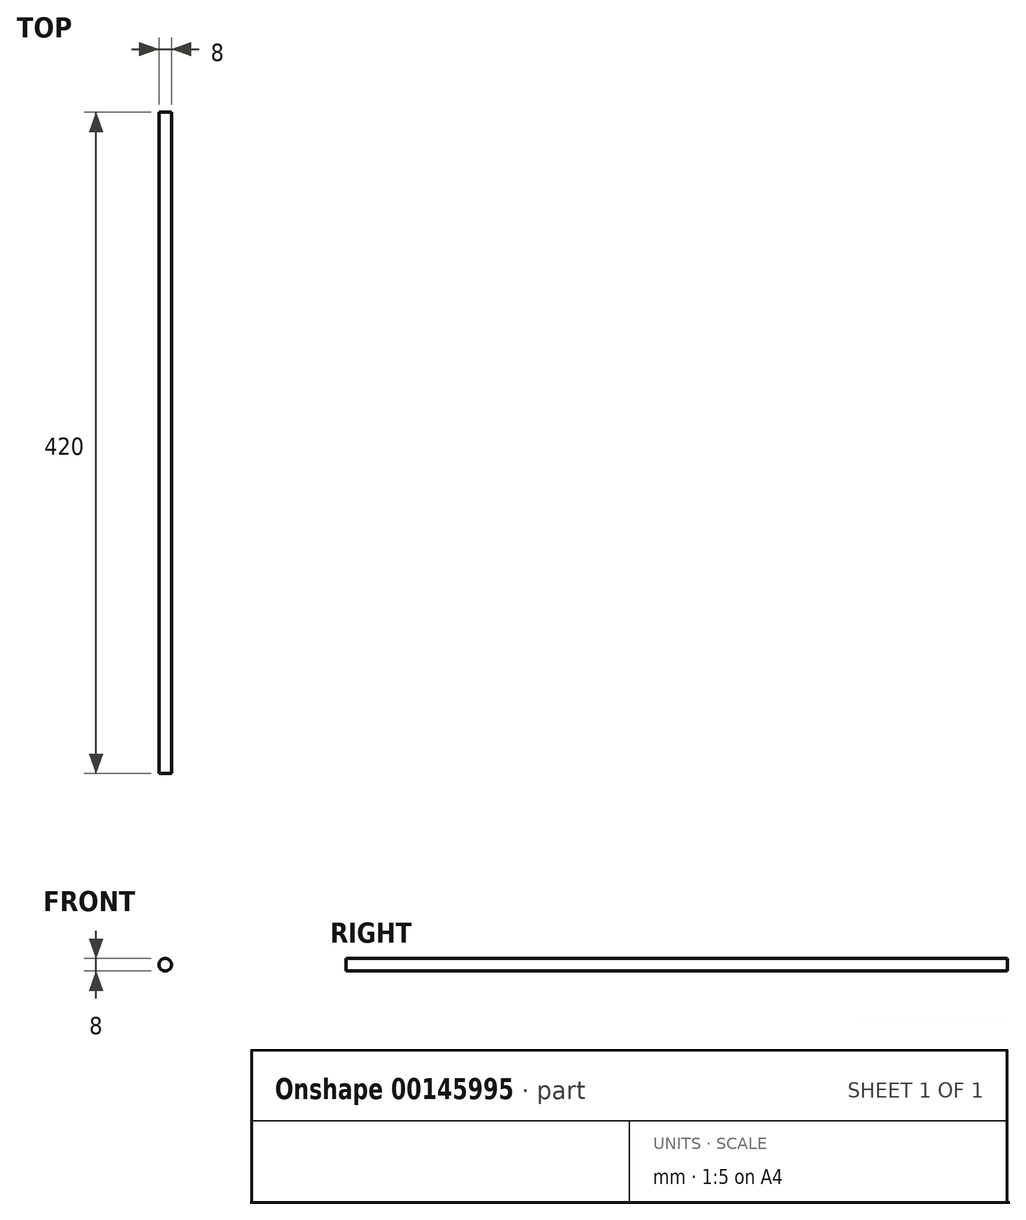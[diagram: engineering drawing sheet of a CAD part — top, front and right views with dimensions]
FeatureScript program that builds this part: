
annotation { "Feature Type Name" : "Feature", "Feature Type Description" : "" }
export const myFeature = defineFeature(function(context is Context, id is Id, definition is map)
    precondition{}
    {
        {
            var Q0;
            Q0=qCreatedBy(makeId("Front.planeOp"),FACE);
            var sketch = newSketch(context, id + "F0", { "sketchPlane" : qUnion([Q0])});
            skCircle(sketch, "E0", {"center": v(0, 0) * mm, "radius": 4 * mm});
            skSolve(sketch);
        }
        {
            var Q0;
            Q0 = qSketchRegion(id + "F0", true);
            extrude(context, id + "F1", {"entities" : qUnion([Q0]), "depth" : 420 * mm});
        }
    });
